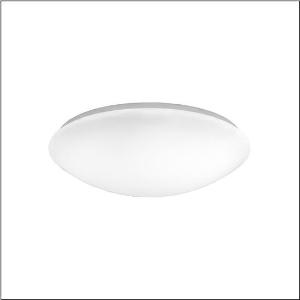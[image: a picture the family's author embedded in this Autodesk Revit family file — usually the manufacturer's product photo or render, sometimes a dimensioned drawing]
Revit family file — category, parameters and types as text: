
# Revit family: round_31_b_5pja230001a
name_source: partatom
category: Lighting Fixtures
units: mm (PartAtom-declared; Revit-internal decimal feet)

## family parameters
Cut with Voids When Loaded = No
Host = Face
Light Source = No
Part Type = Normal
Room Calculation Point = No
Round Connector Dimension = Use Diameter
Shared = No

## types (1)
- --- (1 x LED, 4900 lm, 39 W, 4000K)
    Apparent Load = 39 VA
    CIE Flux Codes = 42 71 89 88 100
    Color Rendering = 80
    Color Temperature = 4000K
    Default Elevation = 1800 mm
    Description = Round 31 B, wall and ceiling luminaire, primary optical cover: enclosure, of PMMA, light emission: direct distribution, primary light characteristic: symmetric, installation type: surface-mounted, LED, rated luminous flux: 4.900lm, luminous efficacy: 126lm/W, light colour: 840, colour temperature: 4000K, with terminal, 3-pole, max. 2.5mm², mains connection: 230V, AC, 50/60Hz, rated input power: 39W, luminaire housing, round, of steel, white, diameter: 464mm, height: 120mm, protection rating (complete): IP40, insulation class (complete): insulation class I (protective earthing), certification: CE, impact resistance: IK02, packaging unit: 1 piece
    Height = 120 mm
    Lamp = 1 x LED
    Lamp Light Flux = 4900 lm
    Lamp Power = 39 W
    Lamp count = 1
    Length = 464 mm
    Luminous efficacy = 126 lm/W
    Manufacturer = Siteco
    ModVariant = No
    Model = 5PJA230001A
    Mounting Place = Ceiling
    Mounting Type = Surface mounted
    Number of Poles = 1
    OnlyDefault = Yes
    Power Factor = 1
    Product Name = Round 31 B
    Product group = wall and ceiling luminaire
    ProductGroupID = 301
    Protection Class = Protection class I
    Protection Degree = IP 40
    RLX_Detail_Level = 1
    RLX_Emergency_Light_Flux = 0 lm
    RLX_Emergency_Type = 0
    RLX_Emergency_Type_DB = No
    RlxData = <blob elided: 13745 chars, md5=740c809c>
    Socket = socket
    Standby Power = 0 W
    System Light Flux = 4900 lm
    System Power = 39 W
    Type Comments = factory setting: luminous flux: 100 % | (ON | ON | ON) | 1050 mA
    Type Image = l_1258313.jpg
    URL = http://relux.com
    VarID = @adj_013673
    Voltage = 0 V
    Weight = 0.00 kg
    Width = 0 mm  [stored 0 ft]

note: [stored X ft] marks values corroborated as IEEE doubles in the binary element streams (Revit-internal decimal feet)

## geometry (parser evidence)
native form markers: Sweep x13
no freeform markers — native parametric forms only
